# Revit family: Hekatron_Rauchwarnmelder_KonexXt CO One_DE_25.01
name_source: partatom
category: Brandmelder
revit_build: Autodesk Revit 2018 (Build: 20170223_1515(x64)
units: mm (PartAtom-declared; Revit-internal decimal feet)

## family parameters
Basisbauteil = Fläche
Beim Laden mit Abzugskörper schneiden = Nein
Bemaßung runder Anschluss = Durchmesser verwenden
Beschriftungsausrichtung beibehalten = Ja
Gemeinsam genutzt = Nein
OmniClass-Nummer = 23.85.30.21
OmniClass-Titel = Environmental Detection/Registration
Raumberechnungspunkt = Nein
Teiletyp = Normal

## types (1)
- KonexXt CO One
    Alarm- & Empfindlichkeitsbereich = ab 50 ppm
    Beschreibung = Der CO-Warnmelder warnt zuverlässig vor gefährlichen CO-Konzentrationen z. B. durch 
Gasthermen, Pelletheitzungen, Kamine, Öfen, Wasserpfeifen (Shishas) und offene Feuerstellen.
Der batteriebetriebene Warnmelder ist mit Langzeit-Sensor und -Batterie mit bis zu 10 Jahren 
Laufzeit ausgestattet. Er kann flexibel entweder an der Wand montiert oder auf dem Tisch 
aufgestellt werden.
    Betriebsspannung = 3 V DC
    Breite (mm) = 112.0
    Farbe = weiß, ähnlich RAL 9003
    Funktionsprinzip = elektrochemischer CO-Sensor
    Height = 110 mm
    Hersteller = Hekatron
    Hoehe (mm) = 110.0
    Lautstaerke DIN-Ton (dB) = 85.0
    Link zu Ausschreibungstext = https://www.meinhplus.de
    Link zu Produktinformation = https://www.hekatron-brandschutz.de
    Link zu ausschreiben.de = https://ausschreiben.de
    Link zum Datenblatt = https://www.hekatron-brandschutz.de
    Material = PC-ABS
    Modell = KonexXt CO One
    Montageart = Aufputz & Tischaufsteller
    Nettogewicht (g) = 186.0
    Schutzart = IP42
    Tiefe (mm) = 31.5
    Typenkommentare = CO-Warnmelder KonexXt CO One
    UB A&S Artikel Nummer = 31-6300003-01-01
    URL = www.hekatron-brandschutz.de
    VdS-Anerkennung = CNPP CERTIFICAT N° 72.23.221
    Version des BIM Objektes = 25.01
    Vorgabe-Ansicht = 1200 mm
    Width = 112 mm
    Zulaessige Umgebungstemperatur = -10 °C bis +40 °C

## geometry (parser evidence)
native form markers: Sweep x1
no freeform markers — native parametric forms only
